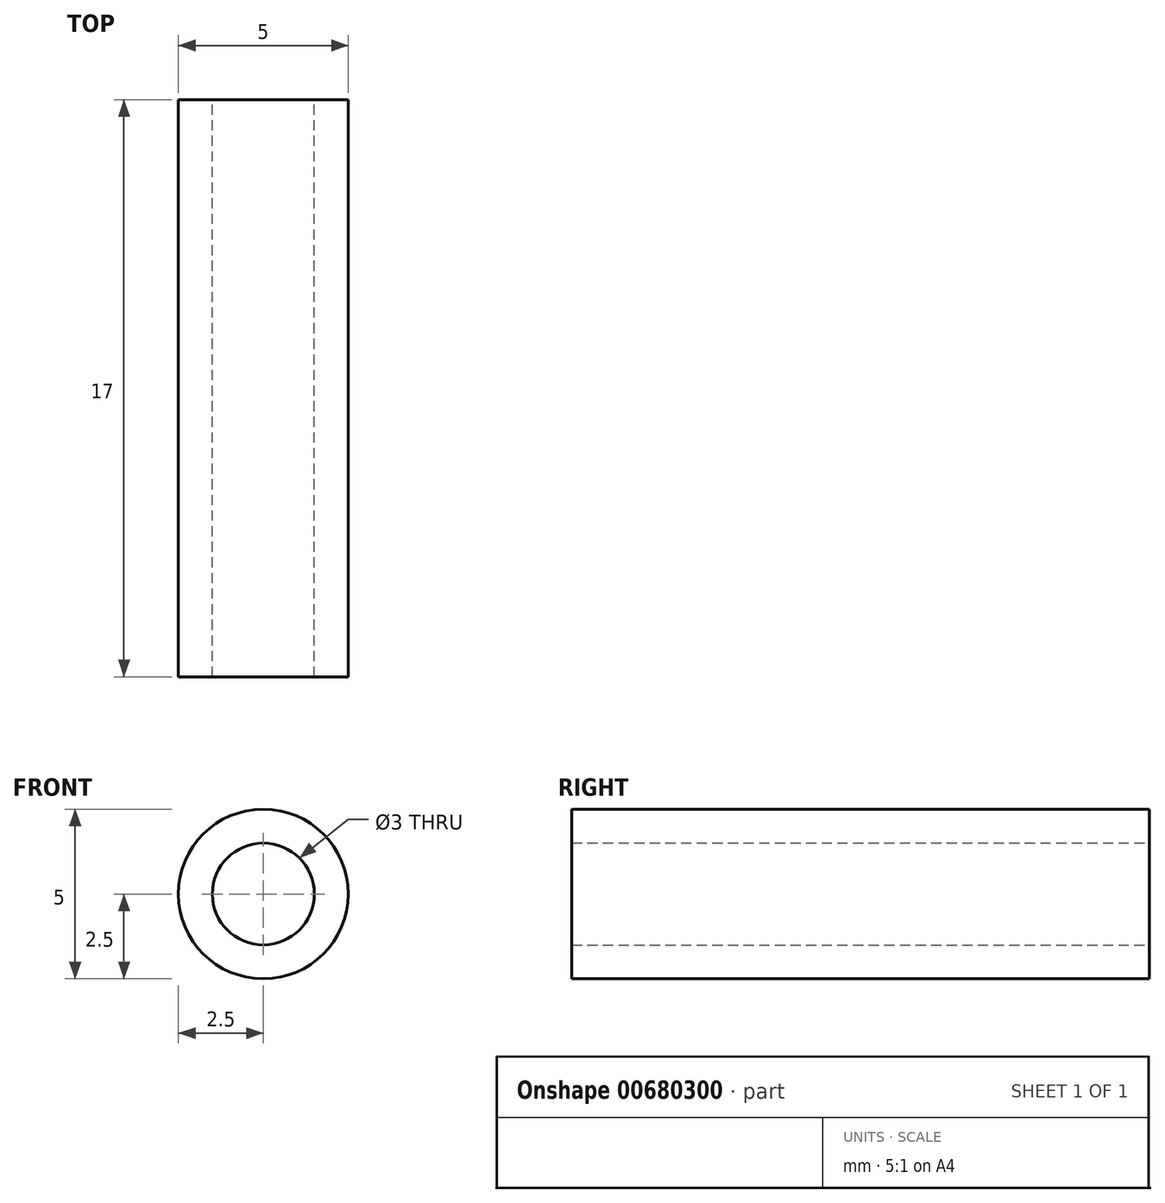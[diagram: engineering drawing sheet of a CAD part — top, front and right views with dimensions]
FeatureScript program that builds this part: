
annotation { "Feature Type Name" : "Feature", "Feature Type Description" : "" }
export const myFeature = defineFeature(function(context is Context, id is Id, definition is map)
    precondition{}
    {
        {
            var Q0;
            Q0=qCreatedBy(makeId("Front.planeOp"),FACE);
            var sketch = newSketch(context, id + "F0", { "sketchPlane" : qUnion([Q0])});
            skCircle(sketch, "E0", {"center": v(0, 0) * mm, "radius": 2.5 * mm});
            skCircle(sketch, "E1", {"center": v(0, 0) * mm, "radius": 1.5 * mm});
            skSolve(sketch);
        }
        {
            var Q0;
            Q0 = qSketchRegion(id + "F0", true);
            extrude(context, id + "F1", {"entities" : qUnion([Q0]), "depth" : 17 * mm, "offsetDistance" : 25 * mm});
        }
    });
